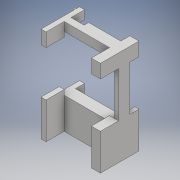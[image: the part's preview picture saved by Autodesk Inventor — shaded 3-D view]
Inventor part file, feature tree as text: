
AUTODESK INVENTOR PART (.ipt)
format: ipt  version: 2017 (Build 210142000, 142)  size: 218,112 bytes
history: native  units: mm
features: sketch x6, extrude x5, other x3
ambient origin geometry x8: Origin, YZ Plane, XZ Plane, XY Plane, X Axis, Y Axis, Z Axis, Center Point
bodies: Solid1 (feature_tree)
feature tree (14):
  other  "120mmLaptopStand-Right.ipt"
  extrude  "Extrusion1"  Depth=29.0mm TaperAngle=0.0deg
  extrude  "Extrusion2"  Depth=10.0mm
  extrude  "Extrusion3"  Depth=10.0mm TaperAngle=0.0deg
  extrude  "Extrusion4"  Depth=20.0mm TaperAngle=0.0deg
  extrude  "Extrusion5"  [1 undecoded]
  other  "Solid1::120mmLaptopStand-Right.ipt"
  other  "TaggingFeature1"
  sketch  "Sketch1"  dims[d0=10.0mm d1=29.0mm d2=0.0mm]
  sketch  "Sketch2"  dims[d3=19.0mm d4=10.0mm]
  sketch  "Sketch3"  dims[d5=20.0mm d6=0.0mm d7=10.0mm d8=0.0mm]
  sketch  "Sketch4"  dims[d9=10.0mm d10=0.0mm d11=20.0mm d12=0.0mm]
  sketch  "Sketch5"
  sketch  "Sketch6"
note: 1 required parameter value undecoded (feature->parameter linkage not recoverable at this tier; creation-order binding heuristic only, values carry confidence <= 0.55)
